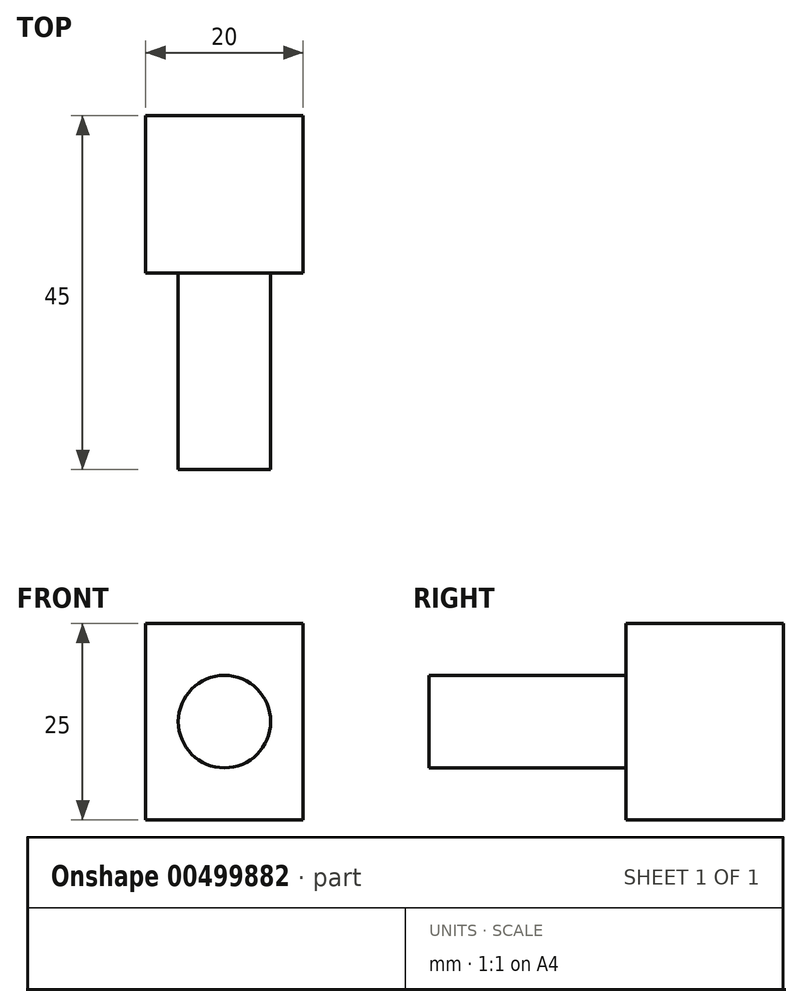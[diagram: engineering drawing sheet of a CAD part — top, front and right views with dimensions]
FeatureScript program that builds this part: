
annotation { "Feature Type Name" : "Feature", "Feature Type Description" : "" }
export const myFeature = defineFeature(function(context is Context, id is Id, definition is map)
    precondition{}
    {
        {
            var Q0;
            Q0=qCreatedBy(makeId("Top.planeOp"),FACE);
            var sketch = newSketch(context, id + "F0", { "sketchPlane" : qUnion([Q0])});
            skLineSegment(sketch, "E0.bottom", {"start": v(0, 0) * mm, "end": v(20, 0) * mm});
            skLineSegment(sketch, "E0.top", {"start": v(0, 20) * mm, "end": v(20, 20) * mm});
            skLineSegment(sketch, "E0.left", {"start": v(0, 0) * mm, "end": v(0, 20) * mm});
            skLineSegment(sketch, "E0.right", {"start": v(20, 0) * mm, "end": v(20, 20) * mm});
            skSolve(sketch);
        }
        {
            var Q0;
            Q0 = qSketchRegion(id + "F0", true);
            extrude(context, id + "F1", {"entities" : qUnion([Q0]), "depth" : 25 * mm});
        }
        {
            var Q0;
            Q0=makeQuery(id+"F1.opExtrude","SWEPT_FACE",FACE,{"disambiguationData":[OSD([sQuery(id+"F0.wireOp",EDGE,"E0.bottom")])]});
            var sketch = newSketch(context, id + "F2", { "sketchPlane" : qUnion([Q0])});
            skCircle(sketch, "E1", {"center": v(10, 12.5) * mm, "radius": 5.87 * mm});
            skPoint(sketch, "E1.centerSnap0", {"position": v(20, 12.5) * mm});
            skPoint(sketch, "E1.centerSnap1", {"position": v(10, 25) * mm});
            skSolve(sketch);
        }
        {
            var Q0;
            Q0 = qSketchRegion(id + "F2", true);
            extrude(context, id + "F3", {"entities" : qUnion([Q0]), "operationType" : NewBodyOperationType.ADD, "depth" : 25 * mm});
        }
    });
